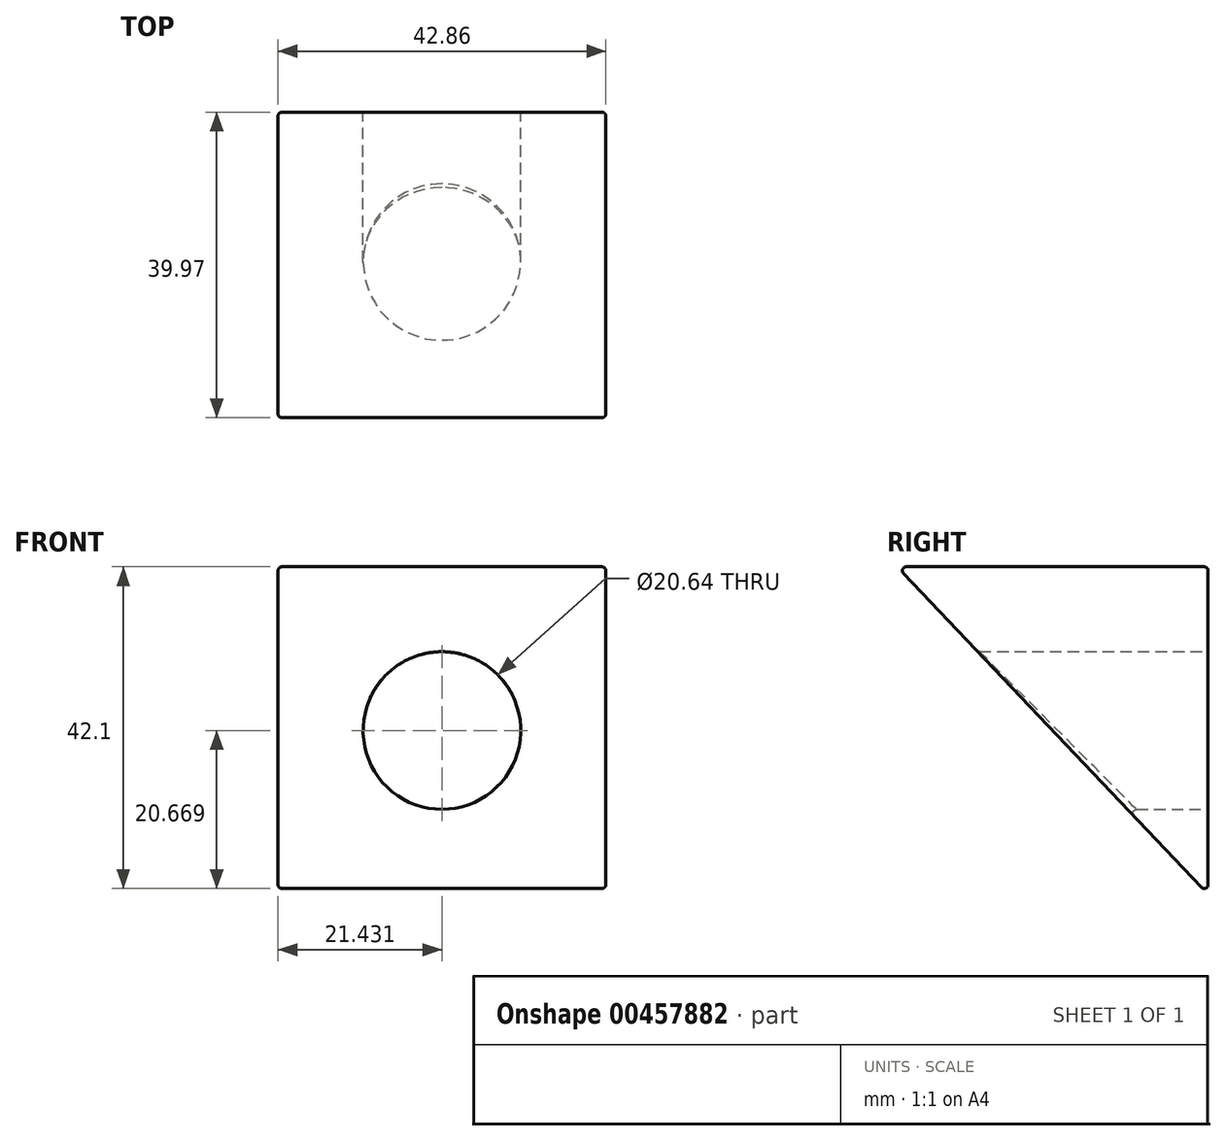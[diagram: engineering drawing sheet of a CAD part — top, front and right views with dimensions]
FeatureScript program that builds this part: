
annotation { "Feature Type Name" : "Feature", "Feature Type Description" : "" }
export const myFeature = defineFeature(function(context is Context, id is Id, definition is map)
    precondition{}
    {
        {
            var Q0;
            Q0=qCreatedBy(makeId("Front.planeOp"),FACE);
            var sketch = newSketch(context, id + "F0", { "sketchPlane" : qUnion([Q0])});
            skLineSegment(sketch, "E0.bottom", {"start": v(0, 0) * mm, "end": v(42.86, 0) * mm});
            skLineSegment(sketch, "E0.top", {"start": v(0, -42.86) * mm, "end": v(42.86, -42.86) * mm});
            skLineSegment(sketch, "E0.left", {"start": v(0, 0) * mm, "end": v(0, -42.86) * mm});
            skLineSegment(sketch, "E0.right", {"start": v(42.86, 0) * mm, "end": v(42.86, -42.86) * mm});
            skLineSegment(sketch, "E1", {"start": v(21.43, 0) * mm, "end": v(21.43, -42.86) * mm, "construction": true});
            skCircle(sketch, "E2", {"center": v(21.43, -21.43) * mm, "radius": 10.32 * mm});
            skSolve(sketch);
        }
        {
            var Q0;
            Q0 = qSketchRegion(id + "F0", true);
            extrude(context, id + "F1", {"entities" : qUnion([Q0]), "depth" : 40.64 * mm});
        }
        {
            var Q0;
            Q0=makeQuery(id+"F1.opExtrude","SWEPT_FACE",FACE,{"disambiguationData":[OSD([sQuery(id+"F0.wireOp",EDGE,"E0.right")])]});
            var sketch = newSketch(context, id + "F2", { "sketchPlane" : qUnion([Q0])});
            skLineSegment(sketch, "E3", {"start": v(-40.64, 0) * mm, "end": v(0, -42.86) * mm});
            skLineSegment(sketch, "E4", {"start": v(-40.64, 0) * mm, "end": v(-40.64, -42.86) * mm});
            skLineSegment(sketch, "E5", {"start": v(-40.64, -42.86) * mm, "end": v(0, -42.86) * mm});
            skSolve(sketch);
        }
        {
            var Q0;
            Q0 = qSketchRegion(id + "F2", true);
            extrude(context, id + "F3", {"entities" : qUnion([Q0]), "operationType" : NewBodyOperationType.REMOVE, "endBound" : BoundingType.THROUGH_ALL, "oppositeDirection" : true, "depth" : 25.4 * mm});
        }
        {
            var Q0;
            Q0=makeQuery(id+"F1.opExtrude","SWEPT_FACE",FACE,{"disambiguationData":[OSD([sQuery(id+"F0.wireOp",EDGE,"E0.right")])]});
            var Q1;
            Q1=makeQuery(id+"F3.boolean.opBoolean","COPY",FACE,{"derivedFrom":makeQuery(id+"F3.opExtrude","SWEPT_FACE",FACE,{"disambiguationData":[OSD([sQuery(id+"F2.wireOp",EDGE,"E3")])]})});
            var Q2;
            Q2=makeQuery(id+"F1.opExtrude","SWEPT_FACE",FACE,{"disambiguationData":[OSD([sQuery(id+"F0.wireOp",EDGE,"E0.left")])]});
            var Q3;
            Q3=makeQuery(id+"F1.opExtrude","CAP_EDGE",EDGE,{"disambiguationData":[OSD([sQuery(id+"F0.wireOp",EDGE,"E0.bottom")])],"isStart":true});
            fillet(context, id + "F4", {"entities" : qUnion([Q0, Q1, Q2, Q3]), "radius" : 0.5 * mm, "tangentPropagation" : true, "allowEdgeOverflow" : false});
        }
    });
